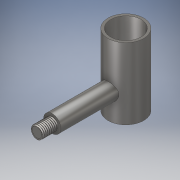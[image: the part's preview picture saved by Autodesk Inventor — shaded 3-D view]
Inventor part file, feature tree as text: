
AUTODESK INVENTOR PART (.ipt)
format: ipt  version: 2019 (Build 230136000, 136)  size: 699,904 bytes
history: native  units: mm
features: sketch x6, extrude x4, revolve x2, projected_geometry x2, plane x1, thread x1, helix x1
ambient origin geometry x8: Origin, YZ Plane, XZ Plane, XY Plane, X Axis, Y Axis, Z Axis, Center Point
bodies: Solid1 (feature_tree), Solid2 (feature_tree)
feature tree (17):
  extrude  "Extrusion1"  Depth=30.0mm
  plane  "Work Plane4"
  sketch  "Sketch2"  dims[d2=70.0mm d3=0.0mm d4=17.5mm]
  extrude  "Extrusion2"  Depth=17.5mm
  extrude  "Extrusion3"  Depth=25.0mm
  extrude  "Extrusion4"  Depth=70.0mm TaperAngle=0.0deg
  thread  "Thread1"  [1 undecoded]
  revolve  "Revolution1"  [1 undecoded]
  revolve  "Revolution2"  [1 undecoded]
  helix  "Coil1"  [1 undecoded]
  sketch  "Sketch1"  dims[d0=35.0mm d1=30.0mm]
  projected_geometry  "Projected Loop1"
  sketch  "Sketch3"  dims[d5=17.0mm d6=25.0mm]
  projected_geometry  "Projected Loop2"
  sketch  "Sketch4"  dims[d7=55.0mm d8=0.0mm d9=70.0mm d10=0.0mm d11=12.0mm]
  sketch  "Sketch5"  dims[d12=15.0mm d13=0.0mm d14=15.0mm d15=0.0mm]
  sketch  "Sketch6"  dims[d16=9.599311mm d17=0.280145mm d18=0.280145mm d21=1.75mm d23=9.599311mm d25=0.0mm d26=0.0mm d27=1.75175mm d28=18.5mm d29=10.0mm d30=0.0mm d31=0.0mm d32=0.0mm d33=0.0mm d34=0.0mm]
note: 4 required parameter values undecoded (feature->parameter linkage not recoverable at this tier; creation-order binding heuristic only, values carry confidence <= 0.55)